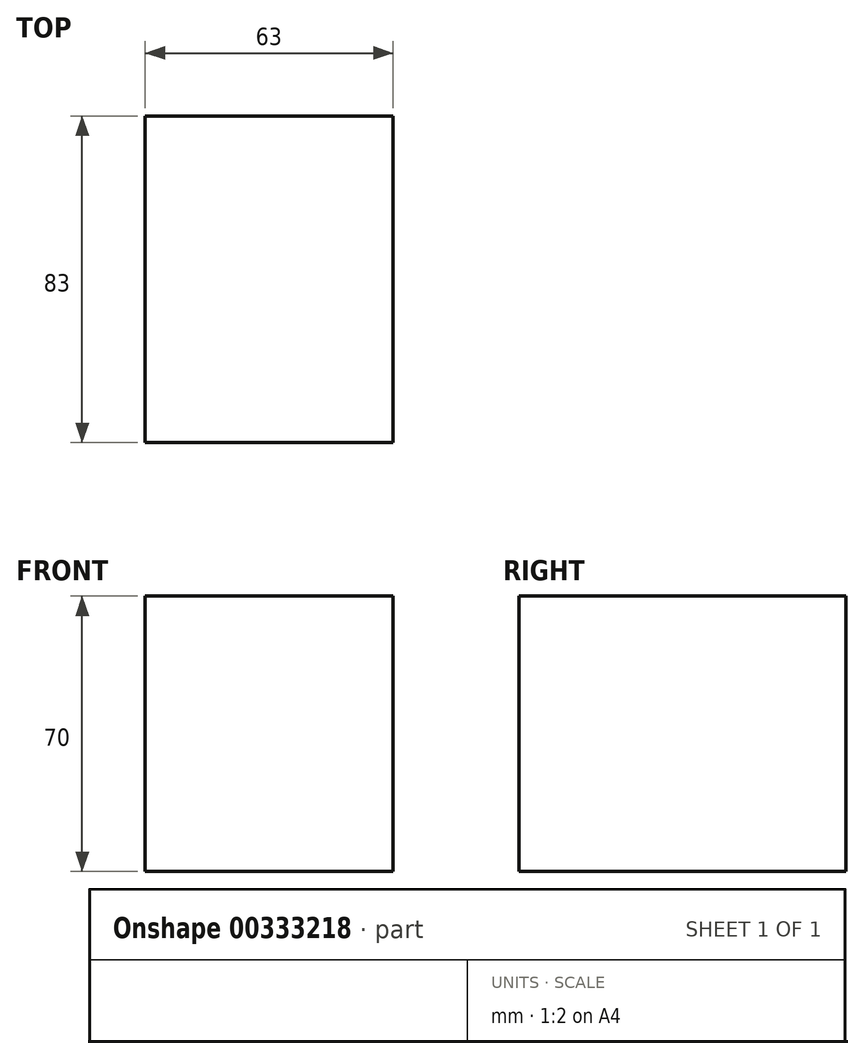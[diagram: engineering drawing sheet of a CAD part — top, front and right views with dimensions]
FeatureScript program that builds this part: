
annotation { "Feature Type Name" : "Feature", "Feature Type Description" : "" }
export const myFeature = defineFeature(function(context is Context, id is Id, definition is map)
    precondition{}
    {
        {
            var Q0;
            Q0=qCreatedBy(makeId("Top.planeOp"),FACE);
            var sketch = newSketch(context, id + "F0", { "sketchPlane" : qUnion([Q0])});
            skLineSegment(sketch, "E0.bottom", {"start": v(31.5, -41.5) * mm, "end": v(-31.5, -41.5) * mm});
            skLineSegment(sketch, "E0.top", {"start": v(31.5, 41.5) * mm, "end": v(-31.5, 41.5) * mm});
            skLineSegment(sketch, "E0.left", {"start": v(31.5, -41.5) * mm, "end": v(31.5, 41.5) * mm});
            skLineSegment(sketch, "E0.right", {"start": v(-31.5, -41.5) * mm, "end": v(-31.5, 41.5) * mm});
            skPoint(sketch, "E0.middle", {"position": v(0, 0) * mm});
            skSolve(sketch);
        }
        {
            var Q0;
            Q0=qSketchRegion(id+"F0",true);
            extrude(context, id + "F1", {"entities" : qUnion([Q0]), "depth" : 70 * mm});
        }
    });
